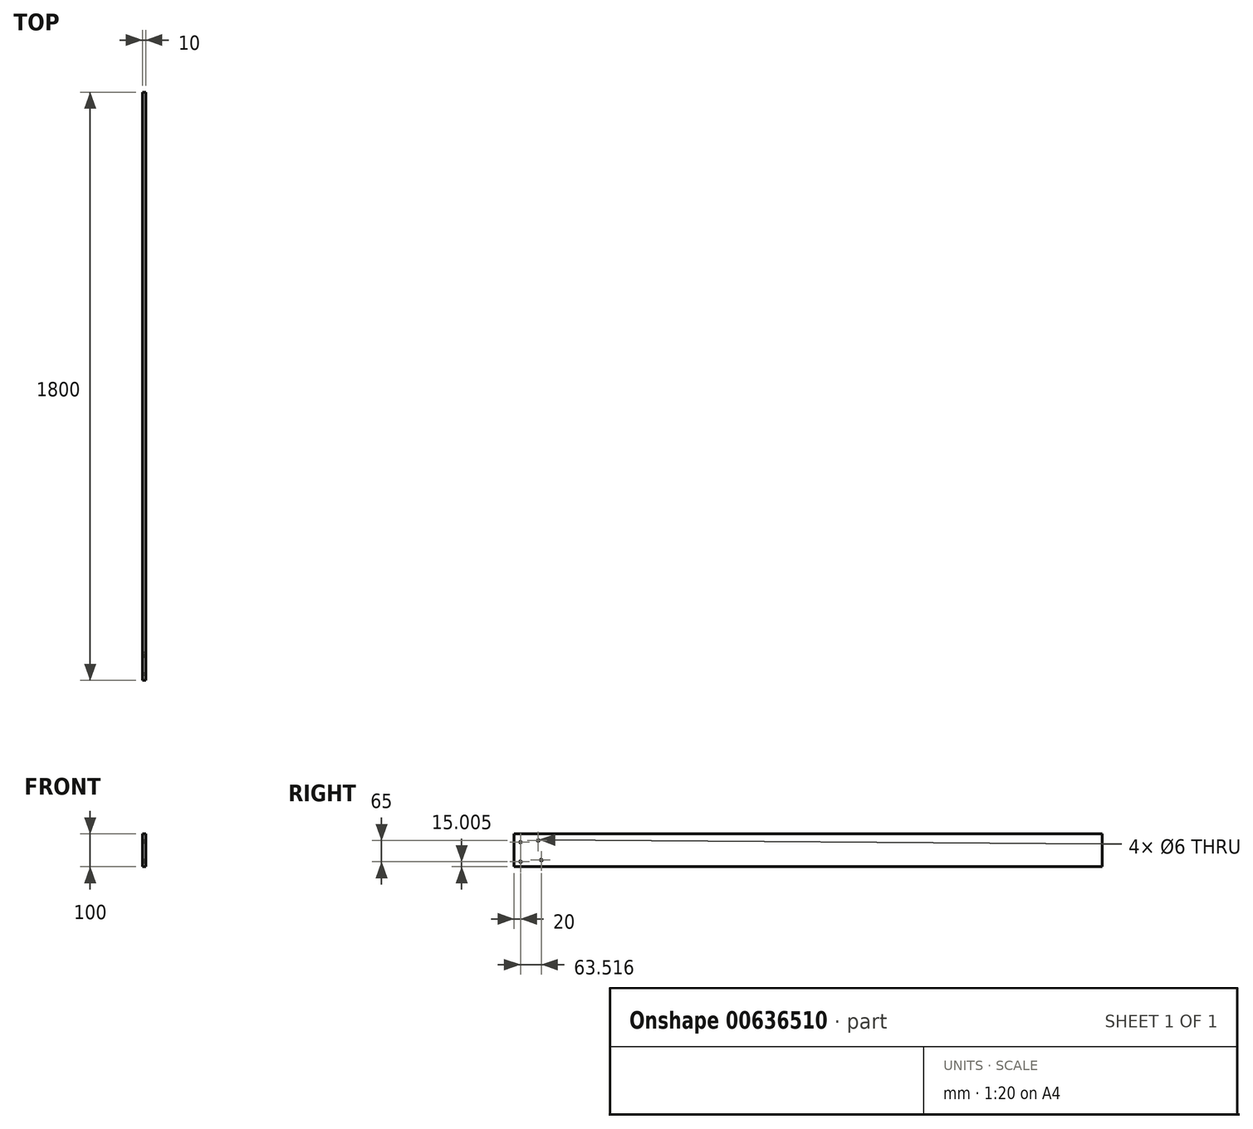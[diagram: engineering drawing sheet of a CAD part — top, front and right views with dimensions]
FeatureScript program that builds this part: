
annotation { "Feature Type Name" : "Feature", "Feature Type Description" : "" }
export const myFeature = defineFeature(function(context is Context, id is Id, definition is map)
    precondition{}
    {
        {
            var Q0;
            Q0=qCreatedBy(makeId("Front.planeOp"),FACE);
            var sketch = newSketch(context, id + "F0", { "sketchPlane" : qUnion([Q0])});
            skLineSegment(sketch, "E0.bottom", {"start": v(9.07, 104.37) * mm, "end": v(19.07, 104.37) * mm});
            skLineSegment(sketch, "E0.top", {"start": v(9.07, 4.37) * mm, "end": v(19.07, 4.37) * mm});
            skLineSegment(sketch, "E0.left", {"start": v(9.07, 104.37) * mm, "end": v(9.07, 4.37) * mm});
            skLineSegment(sketch, "E0.right", {"start": v(19.07, 104.37) * mm, "end": v(19.07, 4.37) * mm});
            skSolve(sketch);
        }
        {
            var Q0;
            Q0=makeQuery(id+"F0.imprint","IMPRINT",FACE,{"disambiguationData":[TD([[makeQuery(id+"F0.imprint","IMPRINT",EDGE,{"derivedFrom":sQuery(id+"F0.wireOp",EDGE,"E0.bottom")}),-1.0]])]});
            extrude(context, id + "F1", {"entities" : qUnion([Q0]), "oppositeDirection" : true, "depth" : 1800 * mm, "offsetDistance" : 25 * mm});
        }
        {
            var Q0;
            Q0=makeQuery(id+"F1.opExtrude","SWEPT_FACE",FACE,{"disambiguationData":[OSD([sQuery(id+"F0.wireOp",EDGE,"E0.right")])]});
            var sketch = newSketch(context, id + "F2", { "sketchPlane" : qUnion([Q0])});
            skPoint(sketch, "E1", {"position": v(20, 79.37) * mm});
            skPoint(sketch, "E2", {"position": v(20, 19.37) * mm});
            skSolve(sketch);
        }
        {
            var Q0;
            {var subQ0=sQuery(id+"F0.wireOp",EDGE,"E0.right");Q0=makeQuery(id+"F2.imprint","IMPRINT",FACE,{"disambiguationData":[TD([[makeQuery(id+"F2.imprint","IMPRINT",EDGE,{"derivedFrom":makeQuery(id+"F1.opExtrude","CAP_EDGE",EDGE,{"disambiguationData":[OSD([subQ0])],"isStart":true})}),1.0]])]});}
            var sketch = newSketch(context, id + "F3", { "sketchPlane" : qUnion([Q0])});
            skPoint(sketch, "E3", {"position": v(74.15, 84.37) * mm});
            skPoint(sketch, "E4", {"position": v(83.52, 24.37) * mm});
            skSolve(sketch);
        }
        {
            var Q0;
            Q0=sQuery(id+"F2.wireOp",VERTEX,"E1");
            var Q1;
            Q1=sQuery(id+"F2.wireOp",VERTEX,"E2");
            var Q2;
            Q2=sQuery(id+"F3.wireOp",VERTEX,"E3");
            var Q3;
            Q3=sQuery(id+"F3.wireOp",VERTEX,"E4");
            var Q4;
            Q4=makeQuery(id+"F1.opExtrude","SWEPT_BODY",BODY,{"disambiguationData":[OSD([sQuery(id+"F0.wireOp",EDGE,"E0.bottom"),sQuery(id+"F0.wireOp",EDGE,"E0.top"),sQuery(id+"F0.wireOp",EDGE,"E0.left"),sQuery(id+"F0.wireOp",EDGE,"E0.right")])]});
            hole(context, id + "F4", {"style" : HoleStyle.SIMPLE, "endStyle" : HoleEndStyle.THROUGH, "holeDiameter" : 6 * mm, "majorDiameter" : 5 * mm, "isTappedThrough" : true, "tappedDepth" : 12 * mm, "tapClearance" : 3, "startFromSketch" : true, "locations" : qUnion([Q0, Q1, Q2, Q3]), "scope" : qUnion([Q4])});
        }
    });
